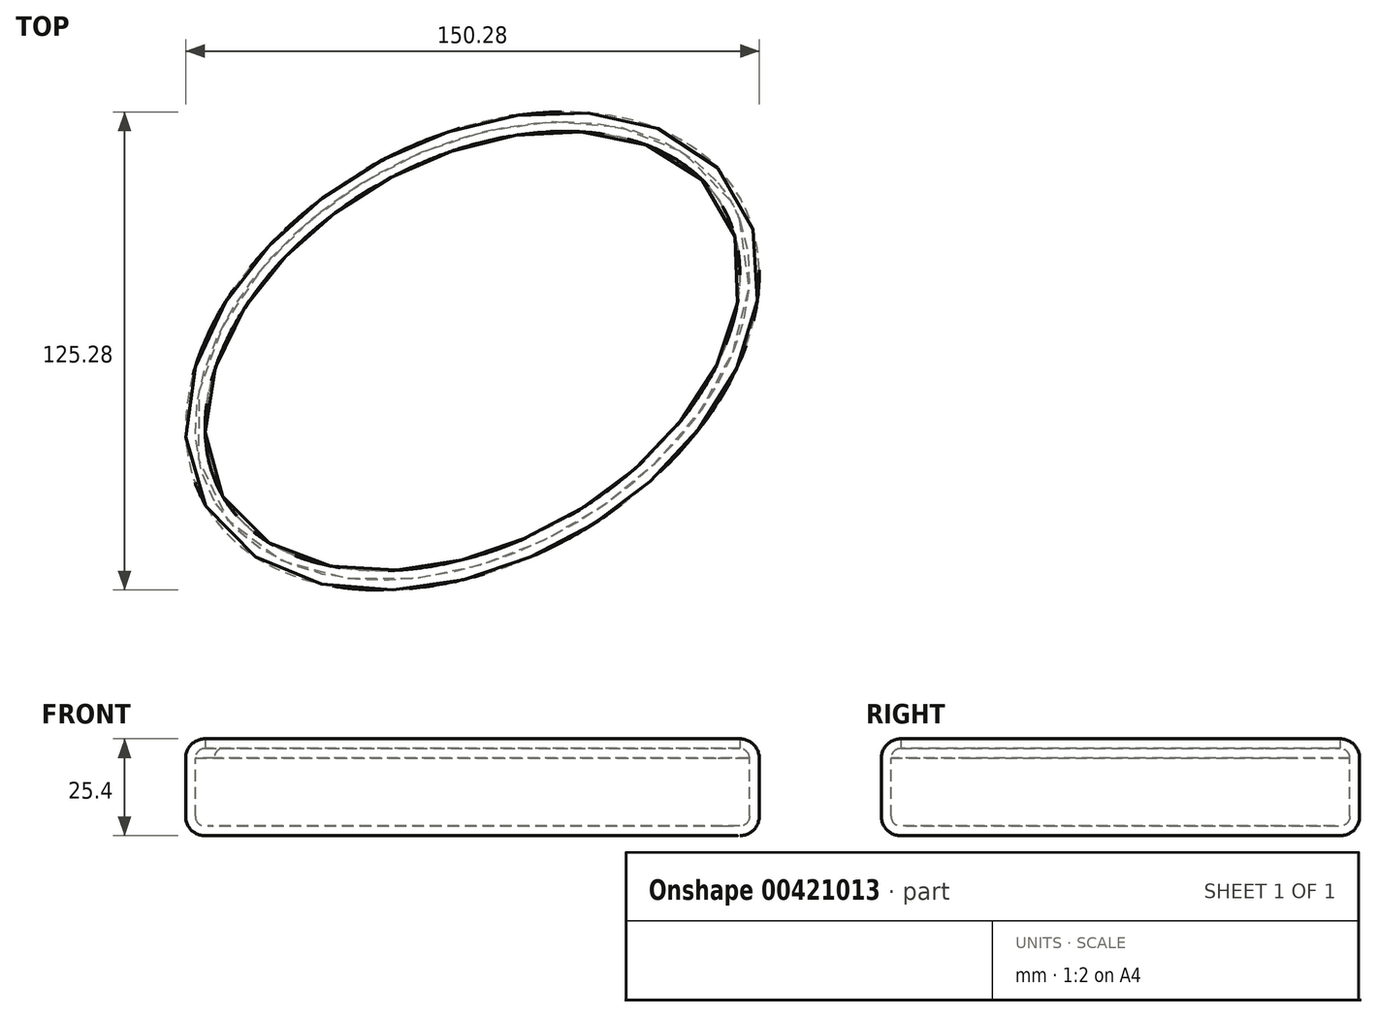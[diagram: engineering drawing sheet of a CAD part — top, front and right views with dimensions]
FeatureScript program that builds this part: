
annotation { "Feature Type Name" : "Feature", "Feature Type Description" : "" }
export const myFeature = defineFeature(function(context is Context, id is Id, definition is map)
    precondition{}
    {
        {
            var Q0;
            Q0=qCreatedBy(makeId("Top.planeOp"),FACE);
            var sketch = newSketch(context, id + "F0", { "sketchPlane" : qUnion([Q0])});
            skEllipse(sketch, "E0", {"center": v(0, 0) * mm, "majorRadius": 55.18 * mm, "minorRadius": 80.78 * mm, "majorAxis": v(-0.5, 0.86)});
            skSolve(sketch);
        }
        {
            var Q0;
            Q0=makeQuery(id+"F0.imprint","IMPRINT",FACE,{"disambiguationData":[TD([[makeQuery(id+"F0.imprint","IMPRINT",EDGE,{"derivedFrom":sQuery(id+"F0.wireOp",EDGE,"E0")}),1.0]])]});
            extrude(context, id + "F1", {"entities" : qUnion([Q0]), "depth" : 25.4 * mm});
        }
        {
            var Q0;
            Q0=makeQuery(id+"F1.opExtrude","CAP_EDGE",EDGE,{"disambiguationData":[OSD([sQuery(id+"F0.wireOp",EDGE,"E0")])],"isStart":false});
            var Q1;
            Q1=makeQuery(id+"F1.opExtrude","SWEPT_FACE",FACE,{"disambiguationData":[OSD([sQuery(id+"F0.wireOp",EDGE,"E0")])]});
            var Q2;
            Q2=makeQuery(id+"F1.opExtrude","CAP_EDGE",EDGE,{"disambiguationData":[OSD([sQuery(id+"F0.wireOp",EDGE,"E0")])],"isStart":true});
            fillet(context, id + "F2", {"entities" : qUnion([Q0, Q1, Q2]), "radius" : 5.08 * mm, "tangentPropagation" : true, "allowEdgeOverflow" : false});
        }
        {
            var Q0;
            Q0=makeQuery(id+"F1.opExtrude","CAP_FACE",FACE,{"disambiguationData":[OSD([sQuery(id+"F0.wireOp",EDGE,"E0")])],"isStart":false});
            shell(context, id + "F3", {"entities" : qUnion([Q0]), "thickness" : 2.54 * mm});
        }
        {
            var Q0;
            {var subQ0=sQuery(id+"F0.wireOp",EDGE,"E0");Q0=makeQuery(id+"F3.opShell","OFFSET_FACE",FACE,{"disambiguationData":[OSD([subQ0]),TDD([makeQuery(id+"F1.opExtrude","CAP_FACE",FACE,{"disambiguationData":[OSD([subQ0])],"isStart":true})])]});}
            var sketch = newSketch(context, id + "F4", { "sketchPlane" : qUnion([Q0])});
            skLineSegment(sketch, "E1", {"start": v(-65, -2.23) * mm, "end": v(-42.21, -16.68) * mm});
            skLineSegment(sketch, "E2", {"start": v(-42.21, -16.68) * mm, "end": v(-57.07, 5.3) * mm});
            skLineSegment(sketch, "E3", {"start": v(-57.07, 5.3) * mm, "end": v(-31.02, -9.15) * mm});
            skLineSegment(sketch, "E4", {"start": v(-31.02, -9.15) * mm, "end": v(-52.8, 13.24) * mm});
            skLineSegment(sketch, "E5", {"start": v(-52.8, 13.24) * mm, "end": v(-23.9, 0) * mm});
            skLineSegment(sketch, "E6", {"start": v(-23.9, 0) * mm, "end": v(-44.86, 22.2) * mm});
            skLineSegment(sketch, "E7", {"start": v(-44.86, 22.2) * mm, "end": v(-18.21, 5.3) * mm});
            skLineSegment(sketch, "E8", {"start": v(-18.21, 5.3) * mm, "end": v(-38.35, 29.73) * mm});
            skLineSegment(sketch, "E9", {"start": v(-38.35, 29.73) * mm, "end": v(-11.28, 14.67) * mm});
            skLineSegment(sketch, "E10", {"start": v(-11.28, 14.67) * mm, "end": v(-28.64, 35.72) * mm});
            skLineSegment(sketch, "E11", {"start": v(-28.64, 35.72) * mm, "end": v(-2.93, 23.21) * mm});
            skLineSegment(sketch, "E12", {"start": v(-2.93, 23.21) * mm, "end": v(-18.78, 42.43) * mm});
            skLineSegment(sketch, "E13", {"start": v(-18.78, 42.43) * mm, "end": v(4.13, 27.91) * mm});
            skLineSegment(sketch, "E14", {"start": v(4.13, 27.91) * mm, "end": v(-6.4, 46.62) * mm});
            skLineSegment(sketch, "E15", {"start": v(-6.4, 46.62) * mm, "end": v(8.87, 30.54) * mm});
            skPoint(sketch, "E16.end.orphan", {"position": v(30.04, 31.56) * mm});
            skPoint(sketch, "E17.start.orphan", {"position": v(13.96, 31.56) * mm});
            skPoint(sketch, "E18.start.orphan", {"position": v(21.7, 31.56) * mm});
            skSolve(sketch);
        }
        {
            var Q0;
            Q0=sQuery(id+"F4.wireOp",EDGE,"E1");
            var Q1;
            Q1=sQuery(id+"F4.wireOp",EDGE,"E2");
            var Q2;
            Q2=sQuery(id+"F4.wireOp",EDGE,"E3");
            var Q3;
            Q3=sQuery(id+"F4.wireOp",EDGE,"E4");
            var Q4;
            Q4=sQuery(id+"F4.wireOp",EDGE,"E6");
            var Q5;
            Q5=sQuery(id+"F4.wireOp",EDGE,"E5");
            var Q6;
            Q6=sQuery(id+"F4.wireOp",EDGE,"E7");
            var Q7;
            Q7=sQuery(id+"F4.wireOp",EDGE,"E8");
            var Q8;
            Q8=sQuery(id+"F4.wireOp",EDGE,"E10");
            var Q9;
            Q9=sQuery(id+"F4.wireOp",EDGE,"E9");
            var Q10;
            Q10=sQuery(id+"F4.wireOp",EDGE,"E11");
            var Q11;
            Q11=sQuery(id+"F4.wireOp",EDGE,"E12");
            var Q12;
            Q12=sQuery(id+"F4.wireOp",EDGE,"E13");
            var Q13;
            Q13=sQuery(id+"F4.wireOp",EDGE,"E14");
            var Q14;
            Q14=sQuery(id+"F4.wireOp",EDGE,"E15");
            extrude(context, id + "F5", {"bodyType" : ToolBodyType.SURFACE, "surfaceEntities" : qUnion([Q0, Q1, Q2, Q3, Q4, Q5, Q6, Q7, Q8, Q9, Q10, Q11, Q12, Q13, Q14]), "depth" : 25.4 * mm});
        }
        {
            var Q0;
            {var subQ0=sQuery(id+"F0.wireOp",EDGE,"E0");Q0=makeQuery(id+"F4.imprint","IMPRINT",FACE,{"disambiguationData":[TD([[makeQuery(id+"F4.imprint","IMPRINT",EDGE,{"derivedFrom":makeQuery(id+"F3.opShell","OFFSET_EDGE",EDGE,{"disambiguationData":[OSD([subQ0]),TDD([makeQuery(id+"F2.opFillet","BLEND_EDGE",EDGE,{"blendedFrom":[makeQuery(id+"F1.opExtrude","CAP_EDGE",EDGE,{"disambiguationData":[OSD([subQ0])],"isStart":true}),makeQuery(id+"F1.opExtrude","CAP_FACE",FACE,{"disambiguationData":[OSD([subQ0])],"isStart":true})],"blendedInto":[makeQuery(id+"F1.opExtrude","CAP_FACE",FACE,{"disambiguationData":[OSD([subQ0])],"isStart":true})]})])]})}),-1.0]])]});}
            var sketch = newSketch(context, id + "F6", { "sketchPlane" : qUnion([Q0])});
            skLineSegment(sketch, "E19", {"start": v(-54.69, -19.84) * mm, "end": v(-60.94, -41.09) * mm});
            skLineSegment(sketch, "E20", {"start": v(-60.94, -41.09) * mm, "end": v(-43.48, -27) * mm});
            skLineSegment(sketch, "E21", {"start": v(-43.48, -27) * mm, "end": v(-51.04, -47.21) * mm});
            skLineSegment(sketch, "E22", {"start": v(-51.04, -47.21) * mm, "end": v(-34.61, -32.48) * mm});
            skLineSegment(sketch, "E23", {"start": v(-34.61, -32.48) * mm, "end": v(-40.6, -51.26) * mm});
            skLineSegment(sketch, "E24", {"start": v(-40.6, -51.26) * mm, "end": v(-24.44, -36.92) * mm});
            skLineSegment(sketch, "E25", {"start": v(-24.44, -36.92) * mm, "end": v(-30.05, -53.86) * mm});
            skLineSegment(sketch, "E26", {"start": v(-30.05, -53.86) * mm, "end": v(-15.84, -38.22) * mm});
            skLineSegment(sketch, "E27", {"start": v(-15.84, -38.22) * mm, "end": v(-18.58, -54.38) * mm});
            skLineSegment(sketch, "E28", {"start": v(-54.69, -19.84) * mm, "end": v(-66.42, -28.31) * mm});
            skSolve(sketch);
        }
        {
            var Q0;
            Q0=sQuery(id+"F6.wireOp",EDGE,"E28");
            var Q1;
            Q1=sQuery(id+"F6.wireOp",EDGE,"E19");
            var Q2;
            Q2=sQuery(id+"F6.wireOp",EDGE,"E20");
            var Q3;
            Q3=sQuery(id+"F6.wireOp",EDGE,"E21");
            var Q4;
            Q4=sQuery(id+"F6.wireOp",EDGE,"E22");
            var Q5;
            Q5=sQuery(id+"F6.wireOp",EDGE,"E23");
            var Q6;
            Q6=sQuery(id+"F6.wireOp",EDGE,"E24");
            var Q7;
            Q7=sQuery(id+"F6.wireOp",EDGE,"E25");
            var Q8;
            Q8=sQuery(id+"F6.wireOp",EDGE,"E26");
            var Q9;
            Q9=sQuery(id+"F6.wireOp",EDGE,"E27");
            extrude(context, id + "F7", {"bodyType" : ToolBodyType.SURFACE, "surfaceEntities" : qUnion([Q0, Q1, Q2, Q3, Q4, Q5, Q6, Q7, Q8, Q9]), "depth" : 25.4 * mm});
        }
        {
            var Q0;
            {var subQ0=sQuery(id+"F0.wireOp",EDGE,"E0");Q0=makeQuery(id+"F4.imprint","IMPRINT",FACE,{"disambiguationData":[TD([[makeQuery(id+"F4.imprint","IMPRINT",EDGE,{"derivedFrom":makeQuery(id+"F3.opShell","OFFSET_EDGE",EDGE,{"disambiguationData":[OSD([subQ0]),TDD([makeQuery(id+"F2.opFillet","BLEND_EDGE",EDGE,{"blendedFrom":[makeQuery(id+"F1.opExtrude","CAP_EDGE",EDGE,{"disambiguationData":[OSD([subQ0])],"isStart":true}),makeQuery(id+"F1.opExtrude","CAP_FACE",FACE,{"disambiguationData":[OSD([subQ0])],"isStart":true})],"blendedInto":[makeQuery(id+"F1.opExtrude","CAP_FACE",FACE,{"disambiguationData":[OSD([subQ0])],"isStart":true})]})])]})}),-1.0]])]});}
            var sketch = newSketch(context, id + "F8", { "sketchPlane" : qUnion([Q0])});
            skLineSegment(sketch, "E29", {"start": v(-66.18, -7.94) * mm, "end": v(-54.47, -13.37) * mm});
            skLineSegment(sketch, "E30", {"start": v(-54.47, -13.37) * mm, "end": v(-67.65, -14.07) * mm});
            skLineSegment(sketch, "E31", {"start": v(-67.65, -14.07) * mm, "end": v(-53.77, -17.63) * mm});
            skLineSegment(sketch, "E32", {"start": v(-53.77, -17.63) * mm, "end": v(-67.73, -23.44) * mm});
            skSolve(sketch);
        }
        {
            var Q0;
            Q0=sQuery(id+"F8.wireOp",EDGE,"E29");
            var Q1;
            Q1=sQuery(id+"F8.wireOp",EDGE,"E30");
            var Q2;
            Q2=sQuery(id+"F8.wireOp",EDGE,"E31");
            var Q3;
            Q3=sQuery(id+"F8.wireOp",EDGE,"E32");
            extrude(context, id + "F9", {"bodyType" : ToolBodyType.SURFACE, "surfaceEntities" : qUnion([Q0, Q1, Q2, Q3]), "depth" : 25.4 * mm});
        }
        {
            var Q0;
            {var subQ0=sQuery(id+"F0.wireOp",EDGE,"E0");Q0=makeQuery(id+"F4.imprint","IMPRINT",FACE,{"disambiguationData":[TD([[makeQuery(id+"F4.imprint","IMPRINT",EDGE,{"derivedFrom":makeQuery(id+"F3.opShell","OFFSET_EDGE",EDGE,{"disambiguationData":[OSD([subQ0]),TDD([makeQuery(id+"F2.opFillet","BLEND_EDGE",EDGE,{"blendedFrom":[makeQuery(id+"F1.opExtrude","CAP_EDGE",EDGE,{"disambiguationData":[OSD([subQ0])],"isStart":true}),makeQuery(id+"F1.opExtrude","CAP_FACE",FACE,{"disambiguationData":[OSD([subQ0])],"isStart":true})],"blendedInto":[makeQuery(id+"F1.opExtrude","CAP_FACE",FACE,{"disambiguationData":[OSD([subQ0])],"isStart":true})]})])]})}),-1.0]])]});}
            var sketch = newSketch(context, id + "F10", { "sketchPlane" : qUnion([Q0])});
            skLineSegment(sketch, "E33", {"start": v(-11.63, -52.95) * mm, "end": v(-12.61, -38.15) * mm});
            skLineSegment(sketch, "E34", {"start": v(-12.61, -38.15) * mm, "end": v(-2.42, -49.77) * mm});
            skLineSegment(sketch, "E35", {"start": v(-2.42, -49.77) * mm, "end": v(-5.6, -36.18) * mm});
            skLineSegment(sketch, "E36", {"start": v(-5.6, -36.18) * mm, "end": v(7.67, -45.94) * mm});
            skLineSegment(sketch, "E37", {"start": v(7.67, -45.94) * mm, "end": v(2.52, -30.92) * mm});
            skLineSegment(sketch, "E38", {"start": v(2.52, -30.92) * mm, "end": v(20.27, -41.44) * mm});
            skLineSegment(sketch, "E39", {"start": v(20.27, -41.44) * mm, "end": v(10.96, -26.97) * mm});
            skLineSegment(sketch, "E40", {"start": v(10.96, -26.97) * mm, "end": v(31.35, -35.96) * mm});
            skLineSegment(sketch, "E41", {"start": v(31.35, -35.96) * mm, "end": v(20.27, -22.26) * mm});
            skLineSegment(sketch, "E42", {"start": v(20.27, -22.26) * mm, "end": v(40, -29.6) * mm});
            skLineSegment(sketch, "E43", {"start": v(40, -29.6) * mm, "end": v(28.82, -17.33) * mm});
            skLineSegment(sketch, "E44", {"start": v(28.82, -17.33) * mm, "end": v(48.56, -21.6) * mm});
            skLineSegment(sketch, "E45", {"start": v(48.56, -21.6) * mm, "end": v(40.55, -11.96) * mm});
            skLineSegment(sketch, "E46", {"start": v(40.55, -11.96) * mm, "end": v(54.36, -13.93) * mm});
            skLineSegment(sketch, "E47", {"start": v(54.36, -13.93) * mm, "end": v(44.5, -4.5) * mm});
            skLineSegment(sketch, "E48", {"start": v(44.5, -4.5) * mm, "end": v(58.64, -6.58) * mm});
            skLineSegment(sketch, "E49", {"start": v(58.64, -6.58) * mm, "end": v(51.4, 2.51) * mm});
            skLineSegment(sketch, "E50", {"start": v(51.4, 2.51) * mm, "end": v(62.26, -1) * mm});
            skLineSegment(sketch, "E51", {"start": v(62.26, -1) * mm, "end": v(56.23, 8) * mm});
            skLineSegment(sketch, "E52", {"start": v(56.23, 8) * mm, "end": v(65.66, 5.8) * mm});
            skSolve(sketch);
        }
        {
            var Q0;
            Q0=sQuery(id+"F10.wireOp",EDGE,"E33");
            var Q1;
            Q1=sQuery(id+"F10.wireOp",EDGE,"E34");
            var Q2;
            Q2=sQuery(id+"F10.wireOp",EDGE,"E35");
            var Q3;
            Q3=sQuery(id+"F10.wireOp",EDGE,"E36");
            var Q4;
            Q4=sQuery(id+"F10.wireOp",EDGE,"E37");
            var Q5;
            Q5=sQuery(id+"F10.wireOp",EDGE,"E38");
            var Q6;
            Q6=sQuery(id+"F10.wireOp",EDGE,"E39");
            var Q7;
            Q7=sQuery(id+"F10.wireOp",EDGE,"E40");
            var Q8;
            Q8=sQuery(id+"F10.wireOp",EDGE,"E41");
            var Q9;
            Q9=sQuery(id+"F10.wireOp",EDGE,"E42");
            var Q10;
            Q10=sQuery(id+"F10.wireOp",EDGE,"E43");
            var Q11;
            Q11=sQuery(id+"F10.wireOp",EDGE,"E44");
            var Q12;
            Q12=sQuery(id+"F10.wireOp",EDGE,"E45");
            var Q13;
            Q13=sQuery(id+"F10.wireOp",EDGE,"E46");
            var Q14;
            Q14=sQuery(id+"F10.wireOp",EDGE,"E47");
            var Q15;
            Q15=sQuery(id+"F10.wireOp",EDGE,"E48");
            var Q16;
            Q16=sQuery(id+"F10.wireOp",EDGE,"E49");
            var Q17;
            Q17=sQuery(id+"F10.wireOp",EDGE,"E50");
            var Q18;
            Q18=sQuery(id+"F10.wireOp",EDGE,"E51");
            var Q19;
            Q19=sQuery(id+"F10.wireOp",EDGE,"E52");
            extrude(context, id + "F11", {"bodyType" : ToolBodyType.SURFACE, "surfaceEntities" : qUnion([Q0, Q1, Q2, Q3, Q4, Q5, Q6, Q7, Q8, Q9, Q10, Q11, Q12, Q13, Q14, Q15, Q16, Q17, Q18, Q19]), "depth" : 25.4 * mm});
        }
        {
            var Q0;
            {var subQ0=sQuery(id+"F0.wireOp",EDGE,"E0");Q0=makeQuery(id+"F4.imprint","IMPRINT",FACE,{"disambiguationData":[TD([[makeQuery(id+"F4.imprint","IMPRINT",EDGE,{"derivedFrom":makeQuery(id+"F3.opShell","OFFSET_EDGE",EDGE,{"disambiguationData":[OSD([subQ0]),TDD([makeQuery(id+"F2.opFillet","BLEND_EDGE",EDGE,{"blendedFrom":[makeQuery(id+"F1.opExtrude","CAP_EDGE",EDGE,{"disambiguationData":[OSD([subQ0])],"isStart":true}),makeQuery(id+"F1.opExtrude","CAP_FACE",FACE,{"disambiguationData":[OSD([subQ0])],"isStart":true})],"blendedInto":[makeQuery(id+"F1.opExtrude","CAP_FACE",FACE,{"disambiguationData":[OSD([subQ0])],"isStart":true})]})])]})}),-1.0]])]});}
            var sketch = newSketch(context, id + "F12", { "sketchPlane" : qUnion([Q0])});
            skLineSegment(sketch, "E53", {"start": v(8.95, 30.62) * mm, "end": v(4.99, 49.33) * mm});
            skLineSegment(sketch, "E54", {"start": v(4.99, 49.33) * mm, "end": v(16.23, 32.19) * mm});
            skLineSegment(sketch, "E55", {"start": v(16.23, 32.19) * mm, "end": v(13.93, 53.1) * mm});
            skLineSegment(sketch, "E56", {"start": v(13.93, 53.1) * mm, "end": v(23.33, 32.37) * mm});
            skLineSegment(sketch, "E57", {"start": v(23.33, 32.37) * mm, "end": v(24.8, 54.5) * mm});
            skLineSegment(sketch, "E58", {"start": v(24.8, 54.5) * mm, "end": v(30.15, 31.63) * mm});
            skLineSegment(sketch, "E59", {"start": v(30.15, 31.63) * mm, "end": v(34.57, 53.66) * mm});
            skLineSegment(sketch, "E60", {"start": v(34.57, 53.66) * mm, "end": v(37.52, 30.99) * mm});
            skLineSegment(sketch, "E61", {"start": v(37.52, 30.99) * mm, "end": v(43.33, 50.99) * mm});
            skLineSegment(sketch, "E62", {"start": v(43.33, 50.99) * mm, "end": v(45.36, 30.62) * mm});
            skLineSegment(sketch, "E63", {"start": v(45.36, 30.62) * mm, "end": v(55.31, 44.17) * mm});
            skSolve(sketch);
        }
        {
            var Q0;
            Q0=sQuery(id+"F12.wireOp",EDGE,"E53");
            var Q1;
            Q1=sQuery(id+"F12.wireOp",EDGE,"E54");
            var Q2;
            Q2=sQuery(id+"F12.wireOp",EDGE,"E55");
            var Q3;
            Q3=sQuery(id+"F12.wireOp",EDGE,"E56");
            var Q4;
            Q4=sQuery(id+"F12.wireOp",EDGE,"E57");
            var Q5;
            Q5=sQuery(id+"F12.wireOp",EDGE,"E58");
            var Q6;
            Q6=sQuery(id+"F12.wireOp",EDGE,"E59");
            var Q7;
            Q7=sQuery(id+"F12.wireOp",EDGE,"E60");
            var Q8;
            Q8=sQuery(id+"F12.wireOp",EDGE,"E61");
            var Q9;
            Q9=sQuery(id+"F12.wireOp",EDGE,"E62");
            var Q10;
            Q10=sQuery(id+"F12.wireOp",EDGE,"E63");
            extrude(context, id + "F13", {"bodyType" : ToolBodyType.SURFACE, "surfaceEntities" : qUnion([Q0, Q1, Q2, Q3, Q4, Q5, Q6, Q7, Q8, Q9, Q10]), "depth" : 25.4 * mm});
        }
        {
            var Q0;
            {var subQ0=sQuery(id+"F0.wireOp",EDGE,"E0");Q0=makeQuery(id+"F4.imprint","IMPRINT",FACE,{"disambiguationData":[TD([[makeQuery(id+"F4.imprint","IMPRINT",EDGE,{"derivedFrom":makeQuery(id+"F3.opShell","OFFSET_EDGE",EDGE,{"disambiguationData":[OSD([subQ0]),TDD([makeQuery(id+"F2.opFillet","BLEND_EDGE",EDGE,{"blendedFrom":[makeQuery(id+"F1.opExtrude","CAP_EDGE",EDGE,{"disambiguationData":[OSD([subQ0])],"isStart":true}),makeQuery(id+"F1.opExtrude","CAP_FACE",FACE,{"disambiguationData":[OSD([subQ0])],"isStart":true})],"blendedInto":[makeQuery(id+"F1.opExtrude","CAP_FACE",FACE,{"disambiguationData":[OSD([subQ0])],"isStart":true})]})])]})}),-1.0]])]});}
            var sketch = newSketch(context, id + "F14", { "sketchPlane" : qUnion([Q0])});
            skLineSegment(sketch, "E64", {"start": v(65.92, 7.41) * mm, "end": v(53.84, 11.65) * mm});
            skLineSegment(sketch, "E65", {"start": v(53.84, 11.65) * mm, "end": v(68.04, 11.65) * mm});
            skLineSegment(sketch, "E66", {"start": v(68.04, 11.65) * mm, "end": v(53.84, 16.72) * mm});
            skLineSegment(sketch, "E67", {"start": v(53.84, 16.72) * mm, "end": v(66.84, 17.92) * mm});
            skLineSegment(sketch, "E68", {"start": v(66.84, 17.92) * mm, "end": v(52.55, 21.88) * mm});
            skLineSegment(sketch, "E69", {"start": v(52.55, 21.88) * mm, "end": v(67.49, 23.82) * mm});
            skLineSegment(sketch, "E70", {"start": v(67.49, 23.82) * mm, "end": v(51.26, 27.6) * mm});
            skLineSegment(sketch, "E71", {"start": v(51.26, 27.6) * mm, "end": v(66.84, 29.07) * mm});
            skLineSegment(sketch, "E72", {"start": v(66.84, 29.07) * mm, "end": v(52.83, 31.75) * mm});
            skLineSegment(sketch, "E73", {"start": v(52.83, 31.75) * mm, "end": v(65.92, 34.33) * mm});
            skLineSegment(sketch, "E74", {"start": v(65.92, 34.33) * mm, "end": v(52.65, 34.33) * mm});
            skLineSegment(sketch, "E75", {"start": v(52.65, 34.33) * mm, "end": v(63.52, 38.48) * mm});
            skLineSegment(sketch, "E76", {"start": v(63.52, 38.48) * mm, "end": v(53.01, 37.37) * mm});
            skSolve(sketch);
        }
        {
            var Q0;
            Q0=sQuery(id+"F14.wireOp",EDGE,"E64");
            var Q1;
            Q1=sQuery(id+"F14.wireOp",EDGE,"E65");
            var Q2;
            Q2=sQuery(id+"F14.wireOp",EDGE,"E66");
            var Q3;
            Q3=sQuery(id+"F14.wireOp",EDGE,"E67");
            var Q4;
            Q4=sQuery(id+"F14.wireOp",EDGE,"E68");
            var Q5;
            Q5=sQuery(id+"F14.wireOp",EDGE,"E69");
            var Q6;
            Q6=sQuery(id+"F14.wireOp",EDGE,"E70");
            var Q7;
            Q7=sQuery(id+"F14.wireOp",EDGE,"E71");
            var Q8;
            Q8=sQuery(id+"F14.wireOp",EDGE,"E72");
            var Q9;
            Q9=sQuery(id+"F14.wireOp",EDGE,"E73");
            var Q10;
            Q10=sQuery(id+"F14.wireOp",EDGE,"E74");
            var Q11;
            Q11=sQuery(id+"F14.wireOp",EDGE,"E75");
            var Q12;
            Q12=sQuery(id+"F14.wireOp",EDGE,"E76");
            extrude(context, id + "F15", {"bodyType" : ToolBodyType.SURFACE, "surfaceEntities" : qUnion([Q0, Q1, Q2, Q3, Q4, Q5, Q6, Q7, Q8, Q9, Q10, Q11, Q12]), "depth" : 25.4 * mm});
        }
    });
